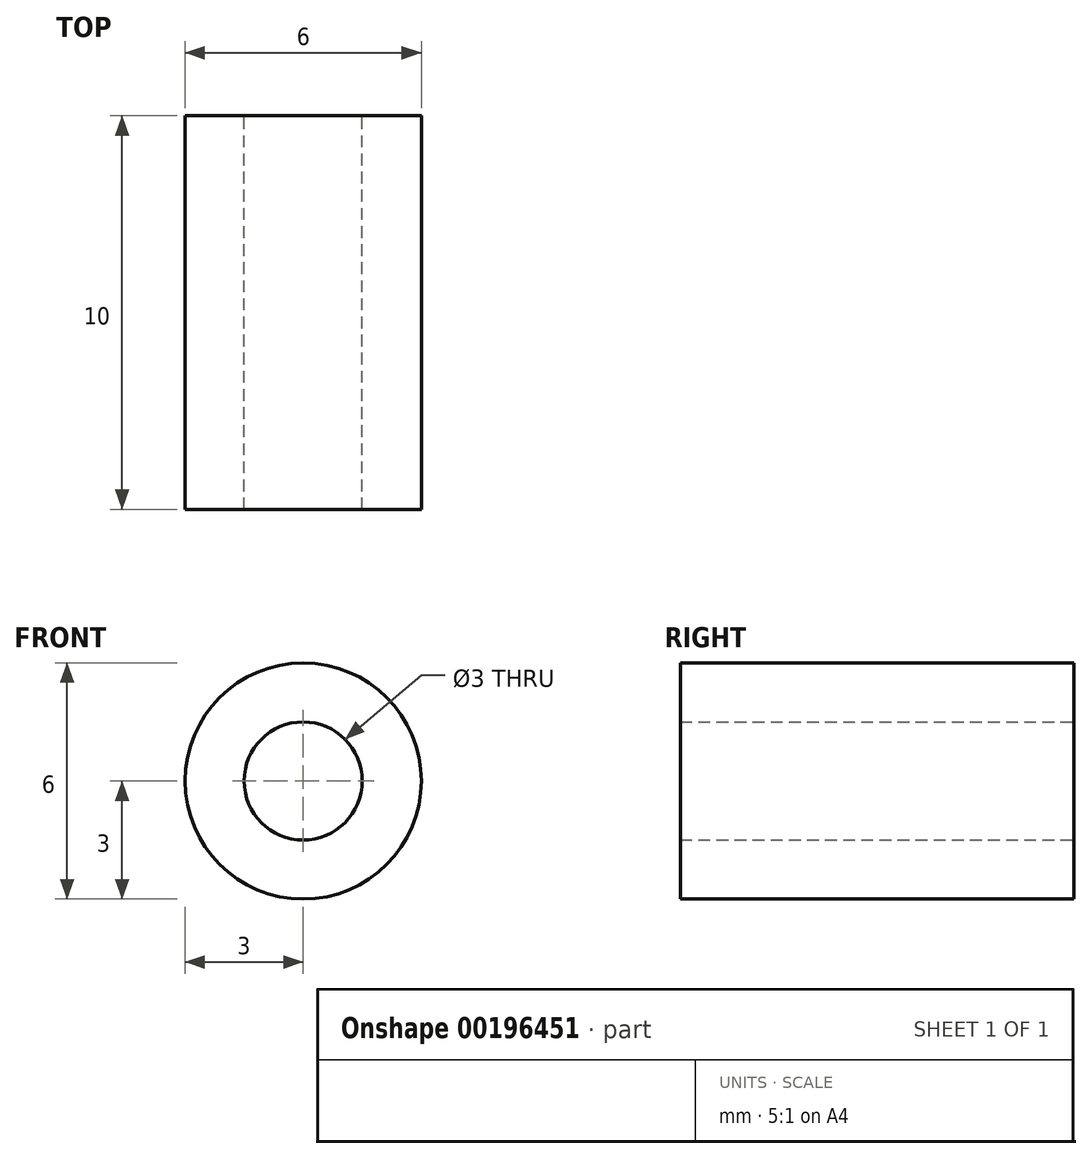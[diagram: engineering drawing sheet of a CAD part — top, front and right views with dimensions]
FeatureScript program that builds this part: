
annotation { "Feature Type Name" : "Feature", "Feature Type Description" : "" }
export const myFeature = defineFeature(function(context is Context, id is Id, definition is map)
    precondition{}
    {
        {
            var Q0;
            Q0=qCreatedBy(makeId("Front.planeOp"),FACE);
            var sketch = newSketch(context, id + "F0", { "sketchPlane" : qUnion([Q0])});
            skCircle(sketch, "E0", {"center": v(0, 0) * mm, "radius": 1.5 * mm});
            skCircle(sketch, "E1", {"center": v(0, 0) * mm, "radius": 3 * mm});
            skSolve(sketch);
        }
        {
            var Q0;
            Q0 = qSketchRegion(id + "F0", true);
            extrude(context, id + "F1", {"entities" : qUnion([Q0]), "depth" : 10 * mm});
        }
    });
